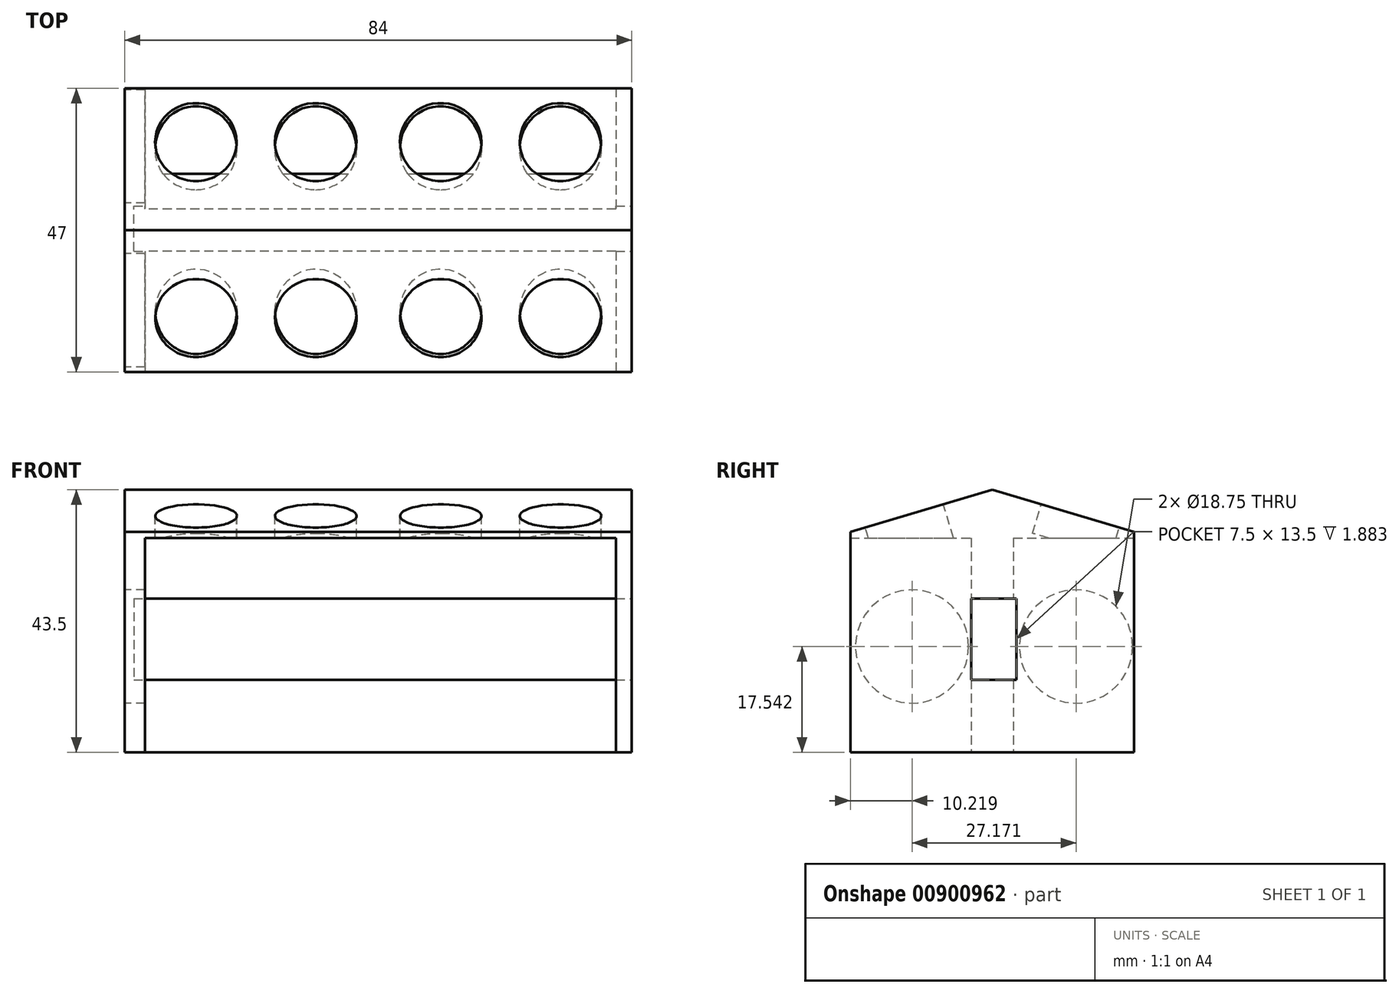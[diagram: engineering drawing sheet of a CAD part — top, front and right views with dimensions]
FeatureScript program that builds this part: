
annotation { "Feature Type Name" : "Feature", "Feature Type Description" : "" }
export const myFeature = defineFeature(function(context is Context, id is Id, definition is map)
    precondition{}
    {
        {
            var Q0;
            Q0=qCreatedBy(makeId("Top.planeOp"),FACE);
            var sketch = newSketch(context, id + "F0", { "sketchPlane" : qUnion([Q0])});
            skLineSegment(sketch, "E0.bottom", {"start": v(-42, 23.5) * mm, "end": v(42, 23.5) * mm});
            skLineSegment(sketch, "E0.top", {"start": v(-42, -23.5) * mm, "end": v(42, -23.5) * mm});
            skLineSegment(sketch, "E0.left", {"start": v(-42, 23.5) * mm, "end": v(-42, -23.5) * mm});
            skLineSegment(sketch, "E0.right", {"start": v(42, 23.5) * mm, "end": v(42, -23.5) * mm});
            skPoint(sketch, "E0.middle", {"position": v(0.6, 0) * mm});
            skSolve(sketch);
        }
        {
            var Q0;
            Q0 = qSketchRegion(id + "F0", true);
            extrude(context, id + "F1", {"entities" : qUnion([Q0]), "depth" : 50 * mm, "offsetDistance" : 25 * mm});
        }
        {
            var Q0;
            Q0=makeQuery(id+"F1.opExtrude","SWEPT_FACE",FACE,{"disambiguationData":[OSD([sQuery(id+"F0.wireOp",EDGE,"E0.right")])]});
            var sketch = newSketch(context, id + "F2", { "sketchPlane" : qUnion([Q0])});
            skLineSegment(sketch, "E1.bottom", {"start": v(-3.5, 32) * mm, "end": v(4, 32) * mm});
            skLineSegment(sketch, "E1.top", {"start": v(-3.5, 18.5) * mm, "end": v(4, 18.5) * mm});
            skLineSegment(sketch, "E1.left", {"start": v(-3.5, 32) * mm, "end": v(-3.5, 18.5) * mm});
            skLineSegment(sketch, "E1.right", {"start": v(4, 32) * mm, "end": v(4, 18.5) * mm});
            skSolve(sketch);
        }
        {
            var Q0;
            Q0 = qSketchRegion(id + "F2", true);
            extrude(context, id + "F3", {"entities" : qUnion([Q0]), "operationType" : NewBodyOperationType.REMOVE, "oppositeDirection" : true, "depth" : 82.5 * mm, "offsetDistance" : 25 * mm});
        }
        {
            var Q0;
            Q0=makeQuery(id+"F1.opExtrude","CAP_FACE",FACE,{"disambiguationData":[OSD([sQuery(id+"F0.wireOp",EDGE,"E0.bottom"),sQuery(id+"F0.wireOp",EDGE,"E0.top"),sQuery(id+"F0.wireOp",EDGE,"E0.left"),sQuery(id+"F0.wireOp",EDGE,"E0.right"),sQuery(id+"F0.wireOp",EDGE,"KOSeehiA-EGKt-3XwV-v0Ph-VlFLIyGEjv8g"),sQuery(id+"F0.wireOp",EDGE,"80754723-99c3-4eb5-9b4f-b7c63d888edb"),sQuery(id+"F0.wireOp",EDGE,"da6288cc-6f90-4600-875a-a1e0f5d1d73f"),sQuery(id+"F0.wireOp",EDGE,"3a80221f-5a08-4d22-b780-35174f4ca253"),sQuery(id+"F0.wireOp",EDGE,"16081203-b5ca-4ee9-9599-153e881b3949"),sQuery(id+"F0.wireOp",EDGE,"7e15494d-697c-4c27-8198-7991228941ef"),sQuery(id+"F0.wireOp",EDGE,"e21bc233-5c4e-4e6b-8942-32940e4b9010"),sQuery(id+"F0.wireOp",EDGE,"7477e375-2078-425e-8677-e3cd12b01fa3")])],"isStart":true});
            var sketch = newSketch(context, id + "F4", { "sketchPlane" : qUnion([Q0])});
            skLineSegment(sketch, "E2.bottom", {"start": v(-38.62, 23.5) * mm, "end": v(39.38, 23.5) * mm});
            skLineSegment(sketch, "E2.top", {"start": v(-38.62, 3.5) * mm, "end": v(39.38, 3.5) * mm});
            skLineSegment(sketch, "E2.left", {"start": v(-38.62, 23.5) * mm, "end": v(-38.62, 3.5) * mm});
            skLineSegment(sketch, "E2.right", {"start": v(39.38, 23.5) * mm, "end": v(39.38, 3.5) * mm});
            skLineSegment(sketch, "E3.bottom", {"start": v(-38.62, -3.5) * mm, "end": v(39.38, -3.5) * mm});
            skLineSegment(sketch, "E3.top", {"start": v(-38.62, -23.5) * mm, "end": v(39.38, -23.5) * mm});
            skLineSegment(sketch, "E3.left", {"start": v(-38.62, -3.5) * mm, "end": v(-38.62, -23.5) * mm});
            skLineSegment(sketch, "E3.right", {"start": v(39.38, -3.5) * mm, "end": v(39.38, -23.5) * mm});
            skSolve(sketch);
        }
        {
            var Q0;
            Q0 = qSketchRegion(id + "F4", true);
            extrude(context, id + "F5", {"entities" : qUnion([Q0]), "operationType" : NewBodyOperationType.REMOVE, "oppositeDirection" : true, "depth" : 42 * mm, "offsetDistance" : 25 * mm});
        }
        {
            var Q0;
            Q0=makeQuery(id+"F1.opExtrude","SWEPT_FACE",FACE,{"disambiguationData":[OSD([sQuery(id+"F0.wireOp",EDGE,"E0.right")])]});
            var sketch = newSketch(context, id + "F6", { "sketchPlane" : qUnion([Q0])});
            skLineSegment(sketch, "E4", {"start": v(0, 50) * mm, "end": v(-23.5, 43) * mm});
            skLineSegment(sketch, "E5", {"start": v(-23.5, 43) * mm, "end": v(-23.5, 50) * mm});
            skLineSegment(sketch, "E6", {"start": v(-23.5, 50) * mm, "end": v(0, 50) * mm});
            skLineSegment(sketch, "E7", {"start": v(0, 50) * mm, "end": v(23.5, 43) * mm});
            skLineSegment(sketch, "E8", {"start": v(23.5, 43) * mm, "end": v(23.5, 50) * mm});
            skLineSegment(sketch, "E9", {"start": v(23.5, 50) * mm, "end": v(0, 50) * mm});
            skSolve(sketch);
        }
        {
            var Q0;
            Q0 = qSketchRegion(id + "F6", true);
            extrude(context, id + "F7", {"entities" : qUnion([Q0]), "operationType" : NewBodyOperationType.REMOVE, "oppositeDirection" : true, "depth" : 84 * mm, "offsetDistance" : 25 * mm});
        }
        {
            var Q0;
            Q0=makeQuery(id+"F7.boolean.opBoolean","COPY",FACE,{"derivedFrom":makeQuery(id+"F7.opExtrude","SWEPT_FACE",FACE,{"disambiguationData":[OSD([sQuery(id+"F6.wireOp",EDGE,"E4")])]})});
            var sketch = newSketch(context, id + "F8", { "sketchPlane" : qUnion([Q0])});
            skCircle(sketch, "E10", {"center": v(-30.18, -0.91) * mm, "radius": 6.75 * mm});
            skCircle(sketch, "E11", {"center": v(-10.35, -0.91) * mm, "radius": 6.75 * mm});
            skCircle(sketch, "E12", {"center": v(10.38, -0.91) * mm, "radius": 6.75 * mm});
            skCircle(sketch, "E13", {"center": v(30.22, -0.91) * mm, "radius": 6.75 * mm});
            skSolve(sketch);
        }
        {
            var Q0;
            Q0 = qSketchRegion(id + "F8", true);
            extrude(context, id + "F9", {"entities" : qUnion([Q0]), "operationType" : NewBodyOperationType.REMOVE, "oppositeDirection" : true, "depth" : 6 * mm, "offsetDistance" : 25 * mm});
        }
        {
            var Q0;
            Q0=makeQuery(id+"F7.boolean.opBoolean","COPY",FACE,{"derivedFrom":makeQuery(id+"F7.opExtrude","SWEPT_FACE",FACE,{"disambiguationData":[OSD([sQuery(id+"F6.wireOp",EDGE,"E7")])]})});
            var sketch = newSketch(context, id + "F10", { "sketchPlane" : qUnion([Q0])});
            skCircle(sketch, "E14", {"center": v(-30.2, 0.95) * mm, "radius": 6.75 * mm});
            skCircle(sketch, "E15", {"center": v(-10.37, 0.95) * mm, "radius": 6.75 * mm});
            skCircle(sketch, "E16", {"center": v(10.35, 0.95) * mm, "radius": 6.75 * mm});
            skCircle(sketch, "E17", {"center": v(30.2, 0.95) * mm, "radius": 6.75 * mm});
            skSolve(sketch);
        }
        {
            var Q0;
            Q0 = qSketchRegion(id + "F10", true);
            extrude(context, id + "F11", {"entities" : qUnion([Q0]), "operationType" : NewBodyOperationType.REMOVE, "oppositeDirection" : true, "depth" : 5 * mm, "offsetDistance" : 25 * mm});
        }
        {
            var Q0;
            Q0=makeQuery(id+"F1.opExtrude","SWEPT_FACE",FACE,{"disambiguationData":[OSD([sQuery(id+"F0.wireOp",EDGE,"E0.left")])]});
            var sketch = newSketch(context, id + "F12", { "sketchPlane" : qUnion([Q0])});
            skCircle(sketch, "E18", {"center": v(-13.9, 24.04) * mm, "radius": 9.38 * mm});
            skCircle(sketch, "E19", {"center": v(13.28, 24.04) * mm, "radius": 9.38 * mm});
            skSolve(sketch);
        }
        {
            var Q0;
            Q0 = qSketchRegion(id + "F12", true);
            extrude(context, id + "F13", {"entities" : qUnion([Q0]), "operationType" : NewBodyOperationType.REMOVE, "oppositeDirection" : true, "depth" : 6 * mm, "offsetDistance" : 25 * mm});
        }
        {
            var Q0;
            Q0=makeQuery(id+"F1.opExtrude","CAP_FACE",FACE,{"disambiguationData":[OSD([sQuery(id+"F0.wireOp",EDGE,"E0.bottom"),sQuery(id+"F0.wireOp",EDGE,"E0.top"),sQuery(id+"F0.wireOp",EDGE,"E0.left"),sQuery(id+"F0.wireOp",EDGE,"E0.right")])],"isStart":true});
            var sketch = newSketch(context, id + "F14", { "sketchPlane" : qUnion([Q0])});
            skLineSegment(sketch, "E20.bottom", {"start": v(-42, 23.5) * mm, "end": v(42, 23.5) * mm});
            skLineSegment(sketch, "E20.top", {"start": v(-42, -23.5) * mm, "end": v(42, -23.5) * mm});
            skLineSegment(sketch, "E20.left", {"start": v(-42, 23.5) * mm, "end": v(-42, -23.5) * mm});
            skLineSegment(sketch, "E20.right", {"start": v(42, 23.5) * mm, "end": v(42, -23.5) * mm});
            skSolve(sketch);
        }
        {
            var Q0;
            Q0 = qSketchRegion(id + "F14", true);
            extrude(context, id + "F15", {"entities" : qUnion([Q0]), "operationType" : NewBodyOperationType.REMOVE, "oppositeDirection" : true, "depth" : 6.5 * mm, "offsetDistance" : 25 * mm});
        }
    });
